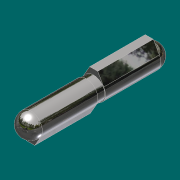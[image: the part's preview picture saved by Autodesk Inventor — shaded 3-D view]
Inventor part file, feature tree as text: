
AUTODESK INVENTOR PART (.ipt)
format: ipt  version: 2017 (Build 210142000, 142)  size: 128,000 bytes
history: native  units: in
note: dims shown in document units (in); Inventor stores cm internally (conversion verified against a paired STEP export)
features: sketch x4, extrude x3, revolve x1
ambient origin geometry x8: Origin, YZ Plane, XZ Plane, XY Plane, X Axis, Y Axis, Z Axis, Center Point
bodies: Solid1 (feature_tree)
feature tree (8):
  extrude  "Extrusion1"  Depth=0.125in TaperAngle=0.0deg
  extrude  "Extrusion2"  Depth=0.9375in TaperAngle=0.0deg
  extrude  "Extrusion3"  TaperAngle=90.0deg  [1 undecoded]
  revolve  "Revolution1"  [1 undecoded]
  sketch  "Sketch1"  dims[d0=0.375in d1=0.125in d2=0.0in]
  sketch  "Sketch2"  dims[d4=60.0deg d5=0.9375in d6=0.0in]
  sketch  "Sketch3"  dims[d7=0.9375in d8=0.0in d9=90.0deg]
  sketch  "Sketch4"  dims[d10=0.4724in d12=0.3937in d13=0.3937in]
note: 2 required parameter values undecoded (feature->parameter linkage not recoverable at this tier; creation-order binding heuristic only, values carry confidence <= 0.55)